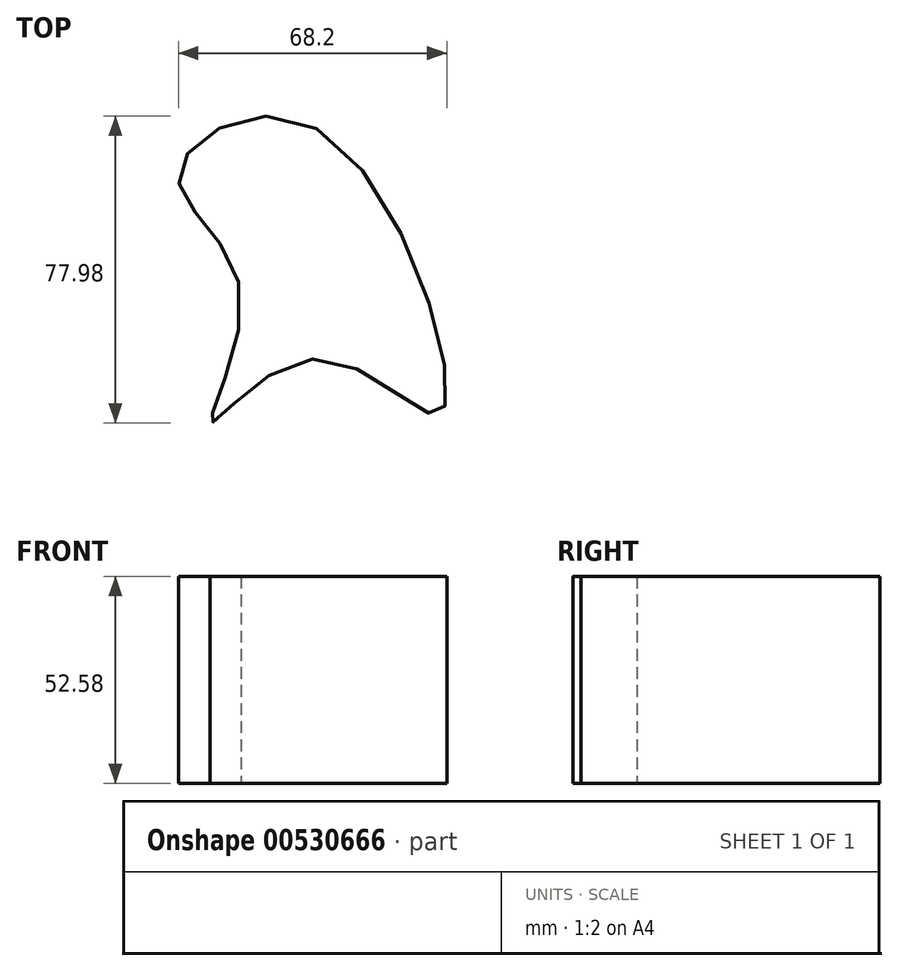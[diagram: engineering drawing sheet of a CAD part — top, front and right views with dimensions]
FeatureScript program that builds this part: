
annotation { "Feature Type Name" : "Feature", "Feature Type Description" : "" }
export const myFeature = defineFeature(function(context is Context, id is Id, definition is map)
    precondition{}
    {
        {
            var Q0;
            Q0=qCreatedBy(makeId("Top.planeOp"),FACE);
            var sketch = newSketch(context, id + "F0", { "sketchPlane" : qUnion([Q0])});
            skFitSpline(sketch, "E0", {"points": [v(0, 40.57) * mm, v(-35.01, 29.09) * mm, v(-19.45, 0) * mm, v(-26.86, -34.27) * mm, v(0, -17.97) * mm, v(31.68, -31.68) * mm, v(0, 40.57) * mm]});
            skSolve(sketch);
        }
        {
            var Q0;
            Q0=makeQuery(id+"F0.imprint","IMPRINT",FACE,{"disambiguationData":[TD([[makeQuery(id+"F0.imprint","IMPRINT",EDGE,{"derivedFrom":sQuery(id+"F0.wireOp",EDGE,"E0")}),1.0]])]});
            extrude(context, id + "F1", {"entities" : qUnion([Q0]), "depth" : 52.58 * mm, "offsetDistance" : 25.4 * mm});
        }
    });
